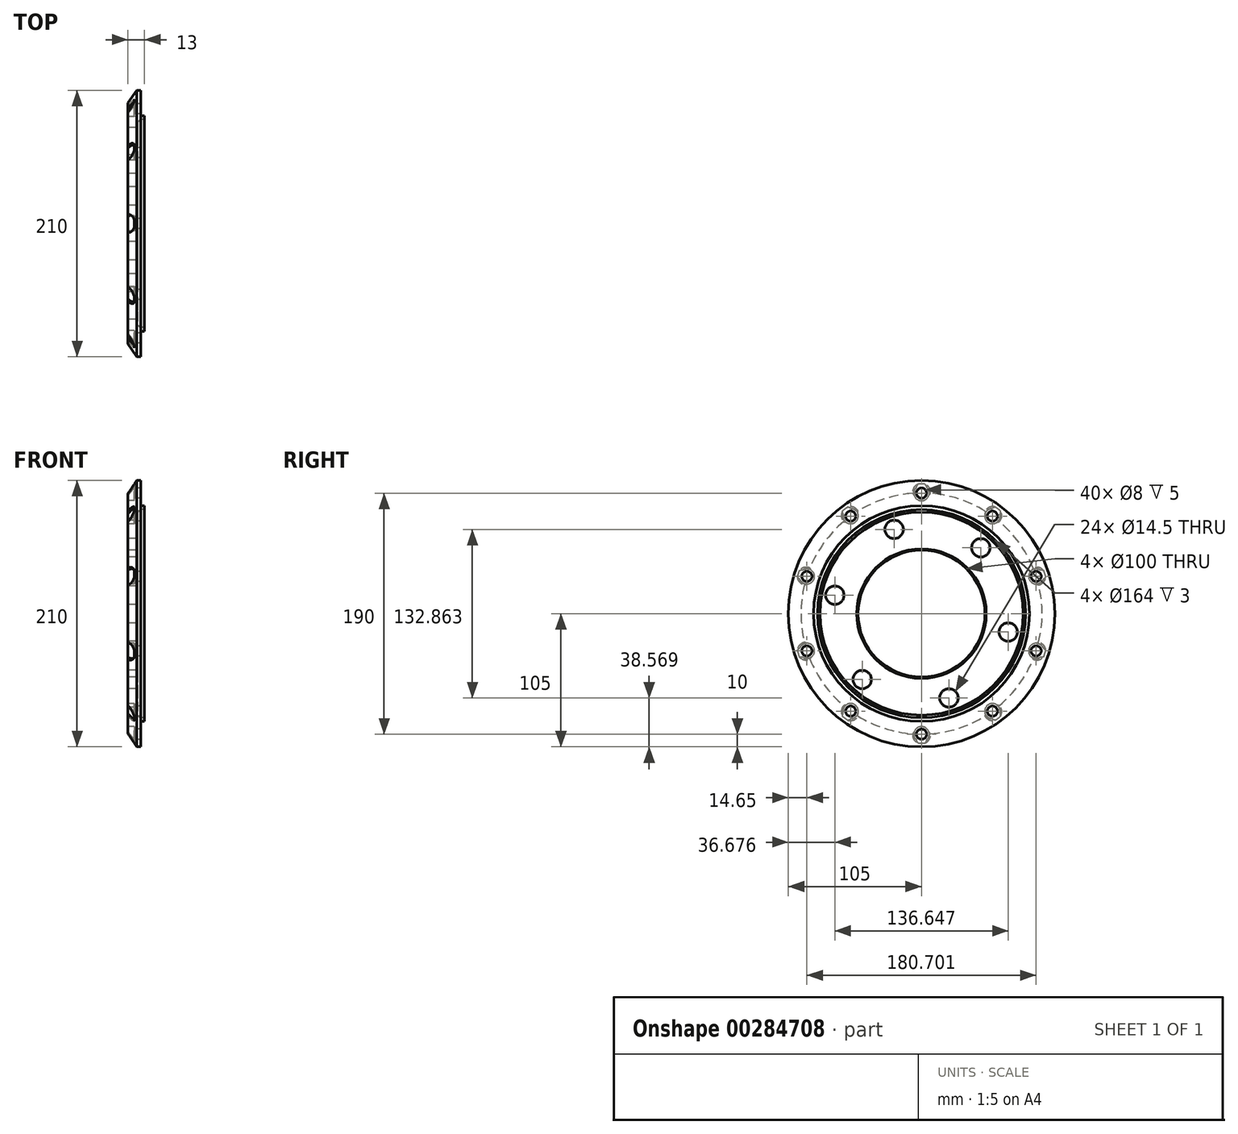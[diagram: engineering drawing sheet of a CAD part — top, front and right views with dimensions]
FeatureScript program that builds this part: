
annotation { "Feature Type Name" : "Feature", "Feature Type Description" : "" }
export const myFeature = defineFeature(function(context is Context, id is Id, definition is map)
    precondition{}
    {
        {
            var Q0;
            Q0=qCreatedBy(makeId("Front.planeOp"),FACE);
            var sketch = newSketch(context, id + "F0", { "sketchPlane" : qUnion([Q0])});
            skLineSegment(sketch, "E0", {"start": v(0, 0) * mm, "end": v(0, 105) * mm});
            skLineSegment(sketch, "E1", {"start": v(0, 105) * mm, "end": v(10, 105) * mm});
            skLineSegment(sketch, "E2", {"start": v(10, 0) * mm, "end": v(10, 105) * mm});
            skLineSegment(sketch, "E3", {"start": v(0, 0) * mm, "end": v(10, 0) * mm});
            skPoint(sketch, "E4", {"position": v(0, 95) * mm});
            skPoint(sketch, "E5", {"position": v(7, 105) * mm});
            skLineSegment(sketch, "E6", {"start": v(7, 105) * mm, "end": v(0, 95) * mm});
            skLineSegment(sketch, "E7", {"start": v(0, 0) * mm, "end": v(0, 50) * mm});
            skLineSegment(sketch, "E8", {"start": v(0, 50) * mm, "end": v(10, 50) * mm});
            skLineSegment(sketch, "E9", {"start": v(13, 82) * mm, "end": v(10, 82) * mm});
            skLineSegment(sketch, "E10", {"start": v(13, 82) * mm, "end": v(13, 85) * mm});
            skLineSegment(sketch, "E11", {"start": v(13, 85) * mm, "end": v(10, 85) * mm});
            skPoint(sketch, "E12", {"position": v(0, 0) * mm});
            skPoint(sketch, "E13", {"position": v(7.5, 0) * mm});
            skLineSegment(sketch, "E14", {"start": v(7.5, 0) * mm, "end": v(7.5, 80) * mm});
            skLineSegment(sketch, "E15", {"start": v(7.5, 80) * mm, "end": v(10, 82) * mm});
            skSolve(sketch);
        }
        {
            var Q0;
            {var subQ2=sQuery(id+"F0.wireOp",EDGE,"K0eps8nP-ykEx-xxXi-aw0d-mbn5K2cVu4G2");Q0=makeQuery(id+"F0.imprint","IMPRINT",FACE,{"disambiguationData":[TD([[makeQuery(id+"F0.imprint","IMPRINT",EDGE,{"derivedFrom":subQ2}),1.0]])]});}
            var Q1;
            {var subQ8=sQuery(id+"F0.wireOp",EDGE,"E6");Q1=makeQuery(id+"F0.imprint","IMPRINT",FACE,{"disambiguationData":[TD([[makeQuery(id+"F0.imprint","IMPRINT",EDGE,{"derivedFrom":subQ8}),1.0]])]});}
            var Q2;
            {var subQ0=sQuery(id+"F0.wireOp",EDGE,"E9");Q2=makeQuery(id+"F0.imprint","IMPRINT",FACE,{"disambiguationData":[TD([[makeQuery(id+"F0.imprint","IMPRINT",EDGE,{"derivedFrom":subQ0}),-1.0]])]});}
            var Q3;
            Q3=sQuery(id+"F0.wireOp",EDGE,"E3");
            revolve(context, id + "F1", {"entities" : qUnion([Q0, Q1, Q2]), "axis" : qUnion([Q3]), "revolveType" : RevolveType.FULL});
        }
        {
            var Q0;
            Q0=makeQuery(id+"F1.opRevolve","SWEPT_FACE",FACE,{"disambiguationData":[OSD([sQuery(id+"F0.wireOp",EDGE,"E0")])]});
            var sketch = newSketch(context, id + "F2", { "sketchPlane" : qUnion([Q0])});
            skCircle(sketch, "E16", {"center": v(0, 0) * mm, "radius": 69.85 * mm, "construction": true});
            skPoint(sketch, "E17", {"position": v(0, 69.85) * mm});
            skCircle(sketch, "E18", {"center": v(0, 0) * mm, "radius": 95 * mm, "construction": true});
            skPoint(sketch, "E19", {"position": v(0, 95) * mm});
            skCircle(sketch, "E20", {"center": v(0, 95) * mm, "radius": 4 * mm});
            skCircle(sketch, "E21.1.0", {"center": v(-55.84, 76.86) * mm, "radius": 4 * mm});
            skCircle(sketch, "E21.2.0", {"center": v(-90.35, 29.36) * mm, "radius": 4 * mm});
            skCircle(sketch, "E21.3.0", {"center": v(-90.35, -29.36) * mm, "radius": 4 * mm});
            skCircle(sketch, "E21.4.0", {"center": v(-55.84, -76.86) * mm, "radius": 4 * mm});
            skCircle(sketch, "E21.5.0", {"center": v(0, -95) * mm, "radius": 4 * mm});
            skCircle(sketch, "E21.6.0", {"center": v(55.84, -76.86) * mm, "radius": 4 * mm});
            skCircle(sketch, "E21.7.0", {"center": v(90.35, -29.36) * mm, "radius": 4 * mm});
            skCircle(sketch, "E21.8.0", {"center": v(90.35, 29.36) * mm, "radius": 4 * mm});
            skCircle(sketch, "E21.9.0", {"center": v(55.84, 76.86) * mm, "radius": 4 * mm});
            skLineSegment(sketch, "E22", {"start": v(0, 0) * mm, "end": v(0, 69.85) * mm, "construction": true});
            skLineSegment(sketch, "E23", {"start": v(0, 0) * mm, "end": v(21.58, 66.43) * mm, "construction": true});
            skCircle(sketch, "E24", {"center": v(21.58, 66.43) * mm, "radius": 7.25 * mm});
            skCircle(sketch, "E25.1.0", {"center": v(-46.74, 51.9) * mm, "radius": 7.25 * mm});
            skCircle(sketch, "E25.2.0", {"center": v(-68.32, -14.52) * mm, "radius": 7.25 * mm});
            skCircle(sketch, "E25.3.0", {"center": v(-21.58, -66.43) * mm, "radius": 7.25 * mm});
            skCircle(sketch, "E25.4.0", {"center": v(46.74, -51.9) * mm, "radius": 7.25 * mm});
            skCircle(sketch, "E26.1.5.0", {"center": v(68.32, 14.52) * mm, "radius": 7.25 * mm});
            skSolve(sketch);
        }
        {
            var Q0;
            Q0 = qSketchRegion(id + "F2", true);
            extrude(context, id + "F3", {"entities" : qUnion([Q0]), "operationType" : NewBodyOperationType.REMOVE, "oppositeDirection" : true, "depth" : 15 * mm});
        }
        {
            var Q0;
            Q0=makeQuery(id+"F1.opRevolve","SWEPT_FACE",FACE,{"disambiguationData":[OSD([sQuery(id+"F0.wireOp",EDGE,"E0")])]});
            var sketch = newSketch(context, id + "F4", { "sketchPlane" : qUnion([Q0])});
            skArc(sketch, "E27.0", {"start": v(-4, 94.92) * mm, "mid": v(0, 91) * mm, "end": v(4, 94.92) * mm});
            skCircle(sketch, "E28", {"center": v(0, 95) * mm, "radius": 6 * mm});
            skCircle(sketch, "E29.1.0", {"center": v(-55.84, 76.86) * mm, "radius": 6 * mm});
            skCircle(sketch, "E29.2.0", {"center": v(-90.35, 29.36) * mm, "radius": 6 * mm});
            skCircle(sketch, "E29.3.0", {"center": v(-90.35, -29.36) * mm, "radius": 6 * mm});
            skCircle(sketch, "E29.4.0", {"center": v(-55.84, -76.86) * mm, "radius": 6 * mm});
            skCircle(sketch, "E29.5.0", {"center": v(0, -95) * mm, "radius": 6 * mm});
            skCircle(sketch, "E29.6.0", {"center": v(55.84, -76.86) * mm, "radius": 6 * mm});
            skCircle(sketch, "E29.7.0", {"center": v(90.35, -29.36) * mm, "radius": 6 * mm});
            skCircle(sketch, "E29.8.0", {"center": v(90.35, 29.36) * mm, "radius": 6 * mm});
            skCircle(sketch, "E29.9.0", {"center": v(55.84, 76.86) * mm, "radius": 6 * mm});
            skPoint(sketch, "E29.center", {"position": v(0, 0) * mm});
            skSolve(sketch);
        }
        {
            var Q0;
            Q0 = qSketchRegion(id + "F4", true);
            extrude(context, id + "F5", {"entities" : qUnion([Q0]), "operationType" : NewBodyOperationType.REMOVE, "oppositeDirection" : true, "depth" : 5 * mm});
        }
        {
            var Q0;
            Q0=makeQuery(id+"F1.opRevolve","SWEPT_EDGE",EDGE,{"disambiguationData":[OSD([sQuery(id+"F0.wireOp",EDGE,"E8"),sQuery(id+"F0.wireOp",EDGE,"E14")])]});
            chamfer(context, id + "F6", {"entities" : qUnion([Q0]), "width" : 1 * mm, "tangentPropagation" : true});
        }
        {
            var Q0;
            Q0=makeQuery(id+"F3.boolean.opBoolean","COPY",EDGE,{"derivedFrom":makeQuery(id+"F3.opExtrude","CAP_EDGE",EDGE,{"disambiguationData":[OSD([sQuery(id+"F2.wireOp",EDGE,"E25.1.0")])],"isStart":true})});
            var Q1;
            Q1=makeQuery(id+"F3.boolean.opBoolean","COPY",EDGE,{"derivedFrom":makeQuery(id+"F3.opExtrude","CAP_EDGE",EDGE,{"disambiguationData":[OSD([sQuery(id+"F2.wireOp",EDGE,"E24")])],"isStart":true})});
            var Q2;
            Q2=makeQuery(id+"F3.boolean.opBoolean","COPY",EDGE,{"derivedFrom":makeQuery(id+"F3.opExtrude","CAP_EDGE",EDGE,{"disambiguationData":[OSD([sQuery(id+"F2.wireOp",EDGE,"E25.4.0")])],"isStart":true})});
            var Q3;
            Q3=makeQuery(id+"F3.boolean.opBoolean","COPY",EDGE,{"derivedFrom":makeQuery(id+"F3.opExtrude","CAP_EDGE",EDGE,{"disambiguationData":[OSD([sQuery(id+"F2.wireOp",EDGE,"E25.3.0")])],"isStart":true})});
            var Q4;
            Q4=makeQuery(id+"F3.boolean.opBoolean","COPY",EDGE,{"derivedFrom":makeQuery(id+"F3.opExtrude","CAP_EDGE",EDGE,{"disambiguationData":[OSD([sQuery(id+"F2.wireOp",EDGE,"E25.2.0")])],"isStart":true})});
            var Q5;
            Q5=makeQuery(id+"F5.boolean.opBoolean","COPY",EDGE,{"derivedFrom":makeQuery(id+"F5.opExtrude","CAP_EDGE",EDGE,{"disambiguationData":[OSD([sQuery(id+"F4.wireOp",EDGE,"E29.3.0")])],"isStart":true})});
            var Q6;
            Q6=makeQuery(id+"F5.boolean.opBoolean","INTERSECT",EDGE,{"derivedFrom":[makeQuery(id+"F1.opRevolve","SWEPT_FACE",FACE,{"disambiguationData":[OSD([sQuery(id+"F0.wireOp",EDGE,"E6")])]}),makeQuery(id+"F5.opExtrude","SWEPT_FACE",FACE,{"disambiguationData":[OSD([sQuery(id+"F4.wireOp",EDGE,"E29.3.0")])]})]});
            var Q7;
            Q7=makeQuery(id+"F5.boolean.opBoolean","COPY",EDGE,{"derivedFrom":makeQuery(id+"F5.opExtrude","CAP_EDGE",EDGE,{"disambiguationData":[OSD([sQuery(id+"F4.wireOp",EDGE,"E29.4.0")])],"isStart":true})});
            var Q8;
            Q8=makeQuery(id+"F5.boolean.opBoolean","INTERSECT",EDGE,{"derivedFrom":[makeQuery(id+"F1.opRevolve","SWEPT_FACE",FACE,{"disambiguationData":[OSD([sQuery(id+"F0.wireOp",EDGE,"E6")])]}),makeQuery(id+"F5.opExtrude","SWEPT_FACE",FACE,{"disambiguationData":[OSD([sQuery(id+"F4.wireOp",EDGE,"E29.4.0")])]})]});
            var Q9;
            Q9=makeQuery(id+"F5.boolean.opBoolean","COPY",EDGE,{"derivedFrom":makeQuery(id+"F5.opExtrude","CAP_EDGE",EDGE,{"disambiguationData":[OSD([sQuery(id+"F4.wireOp",EDGE,"E29.5.0")])],"isStart":true})});
            var Q10;
            Q10=makeQuery(id+"F5.boolean.opBoolean","INTERSECT",EDGE,{"derivedFrom":[makeQuery(id+"F1.opRevolve","SWEPT_FACE",FACE,{"disambiguationData":[OSD([sQuery(id+"F0.wireOp",EDGE,"E6")])]}),makeQuery(id+"F5.opExtrude","SWEPT_FACE",FACE,{"disambiguationData":[OSD([sQuery(id+"F4.wireOp",EDGE,"E29.5.0")])]})]});
            var Q11;
            Q11=makeQuery(id+"F5.boolean.opBoolean","COPY",EDGE,{"derivedFrom":makeQuery(id+"F5.opExtrude","CAP_EDGE",EDGE,{"disambiguationData":[OSD([sQuery(id+"F4.wireOp",EDGE,"E29.6.0")])],"isStart":true})});
            var Q12;
            Q12=makeQuery(id+"F5.boolean.opBoolean","INTERSECT",EDGE,{"derivedFrom":[makeQuery(id+"F1.opRevolve","SWEPT_FACE",FACE,{"disambiguationData":[OSD([sQuery(id+"F0.wireOp",EDGE,"E6")])]}),makeQuery(id+"F5.opExtrude","SWEPT_FACE",FACE,{"disambiguationData":[OSD([sQuery(id+"F4.wireOp",EDGE,"E29.6.0")])]})]});
            var Q13;
            Q13=makeQuery(id+"F5.boolean.opBoolean","COPY",EDGE,{"derivedFrom":makeQuery(id+"F5.opExtrude","CAP_EDGE",EDGE,{"disambiguationData":[OSD([sQuery(id+"F4.wireOp",EDGE,"E29.7.0")])],"isStart":true})});
            var Q14;
            Q14=makeQuery(id+"F5.boolean.opBoolean","INTERSECT",EDGE,{"derivedFrom":[makeQuery(id+"F1.opRevolve","SWEPT_FACE",FACE,{"disambiguationData":[OSD([sQuery(id+"F0.wireOp",EDGE,"E6")])]}),makeQuery(id+"F5.opExtrude","SWEPT_FACE",FACE,{"disambiguationData":[OSD([sQuery(id+"F4.wireOp",EDGE,"E29.7.0")])]})]});
            var Q15;
            Q15=makeQuery(id+"F5.boolean.opBoolean","COPY",EDGE,{"derivedFrom":makeQuery(id+"F5.opExtrude","CAP_EDGE",EDGE,{"disambiguationData":[OSD([sQuery(id+"F4.wireOp",EDGE,"E29.8.0")])],"isStart":true})});
            var Q16;
            Q16=makeQuery(id+"F5.boolean.opBoolean","INTERSECT",EDGE,{"derivedFrom":[makeQuery(id+"F1.opRevolve","SWEPT_FACE",FACE,{"disambiguationData":[OSD([sQuery(id+"F0.wireOp",EDGE,"E6")])]}),makeQuery(id+"F5.opExtrude","SWEPT_FACE",FACE,{"disambiguationData":[OSD([sQuery(id+"F4.wireOp",EDGE,"E29.8.0")])]})]});
            var Q17;
            Q17=makeQuery(id+"F5.boolean.opBoolean","INTERSECT",EDGE,{"derivedFrom":[makeQuery(id+"F1.opRevolve","SWEPT_FACE",FACE,{"disambiguationData":[OSD([sQuery(id+"F0.wireOp",EDGE,"E6")])]}),makeQuery(id+"F5.opExtrude","SWEPT_FACE",FACE,{"disambiguationData":[OSD([sQuery(id+"F4.wireOp",EDGE,"E29.9.0")])]})]});
            var Q18;
            Q18=makeQuery(id+"F5.boolean.opBoolean","COPY",EDGE,{"derivedFrom":makeQuery(id+"F5.opExtrude","CAP_EDGE",EDGE,{"disambiguationData":[OSD([sQuery(id+"F4.wireOp",EDGE,"E29.9.0")])],"isStart":true})});
            var Q19;
            Q19=makeQuery(id+"F5.boolean.opBoolean","INTERSECT",EDGE,{"derivedFrom":[makeQuery(id+"F1.opRevolve","SWEPT_FACE",FACE,{"disambiguationData":[OSD([sQuery(id+"F0.wireOp",EDGE,"E6")])]}),makeQuery(id+"F5.opExtrude","SWEPT_FACE",FACE,{"disambiguationData":[OSD([sQuery(id+"F4.wireOp",EDGE,"E28")])]})]});
            var Q20;
            Q20=makeQuery(id+"F5.boolean.opBoolean","COPY",EDGE,{"derivedFrom":makeQuery(id+"F5.opExtrude","CAP_EDGE",EDGE,{"disambiguationData":[OSD([sQuery(id+"F4.wireOp",EDGE,"E28")])],"isStart":true})});
            var Q21;
            Q21=makeQuery(id+"F5.boolean.opBoolean","INTERSECT",EDGE,{"derivedFrom":[makeQuery(id+"F1.opRevolve","SWEPT_FACE",FACE,{"disambiguationData":[OSD([sQuery(id+"F0.wireOp",EDGE,"E6")])]}),makeQuery(id+"F5.opExtrude","SWEPT_FACE",FACE,{"disambiguationData":[OSD([sQuery(id+"F4.wireOp",EDGE,"E29.1.0")])]})]});
            var Q22;
            Q22=makeQuery(id+"F5.boolean.opBoolean","COPY",EDGE,{"derivedFrom":makeQuery(id+"F5.opExtrude","CAP_EDGE",EDGE,{"disambiguationData":[OSD([sQuery(id+"F4.wireOp",EDGE,"E29.1.0")])],"isStart":true})});
            var Q23;
            Q23=makeQuery(id+"F5.boolean.opBoolean","COPY",EDGE,{"derivedFrom":makeQuery(id+"F5.opExtrude","CAP_EDGE",EDGE,{"disambiguationData":[OSD([sQuery(id+"F4.wireOp",EDGE,"E29.2.0")])],"isStart":true})});
            var Q24;
            Q24=makeQuery(id+"F5.boolean.opBoolean","INTERSECT",EDGE,{"derivedFrom":[makeQuery(id+"F1.opRevolve","SWEPT_FACE",FACE,{"disambiguationData":[OSD([sQuery(id+"F0.wireOp",EDGE,"E6")])]}),makeQuery(id+"F5.opExtrude","SWEPT_FACE",FACE,{"disambiguationData":[OSD([sQuery(id+"F4.wireOp",EDGE,"E29.2.0")])]})]});
            chamfer(context, id + "F7", {"entities" : qUnion([Q0, Q1, Q2, Q3, Q4, Q5, Q6, Q7, Q8, Q9, Q10, Q11, Q12, Q13, Q14, Q15, Q16, Q17, Q18, Q19, Q20, Q21, Q22, Q23, Q24]), "width" : 1 * mm, "tangentPropagation" : true});
        }
    });
